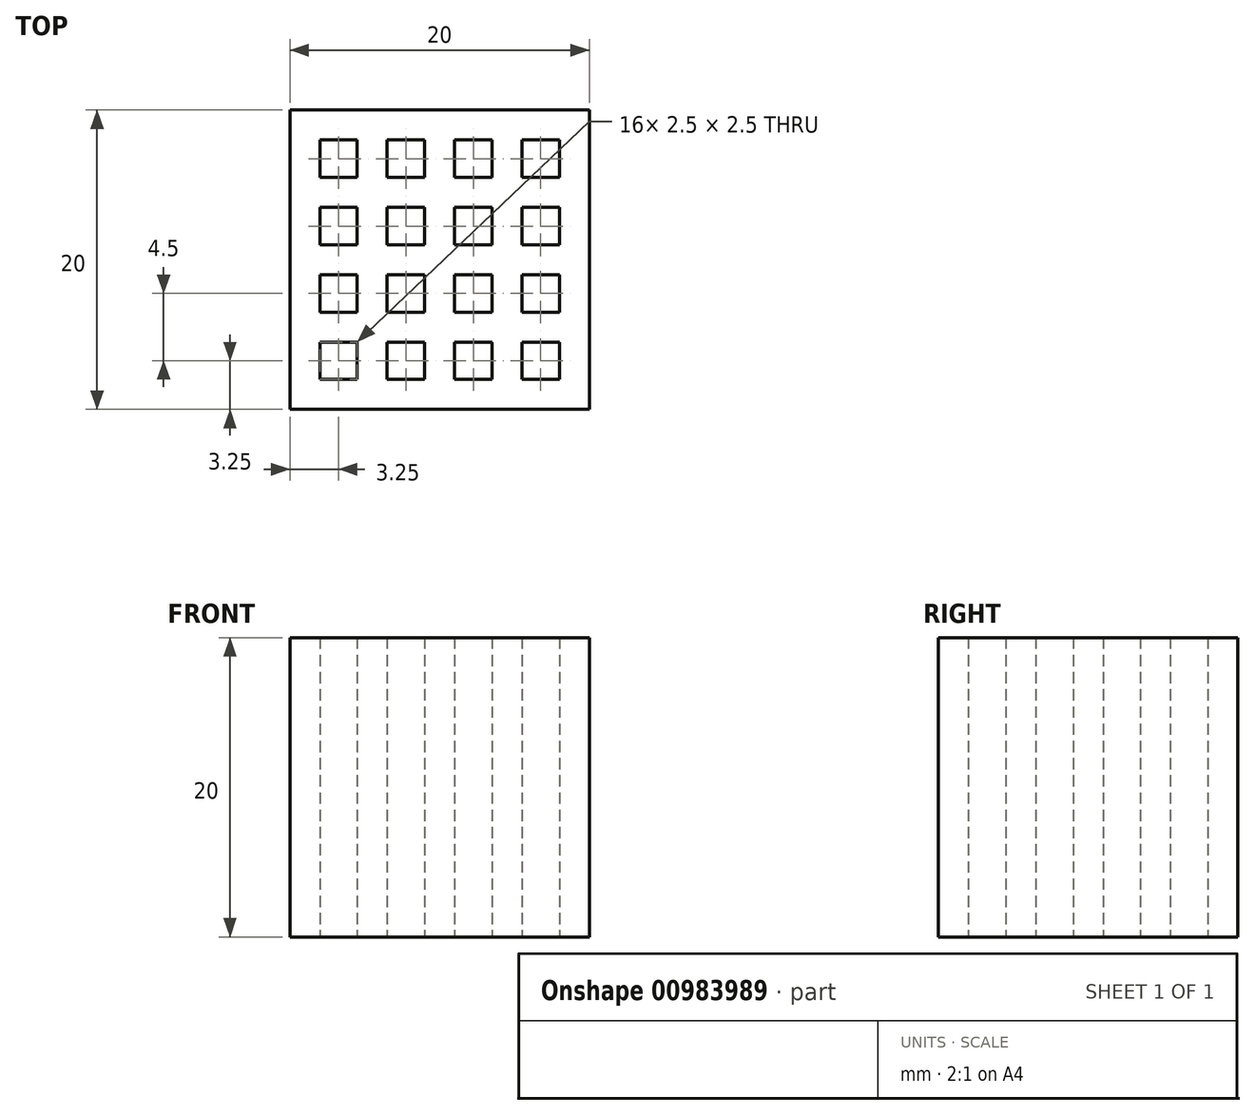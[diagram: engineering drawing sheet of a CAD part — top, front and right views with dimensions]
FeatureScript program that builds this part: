
annotation { "Feature Type Name" : "Feature", "Feature Type Description" : "" }
export const myFeature = defineFeature(function(context is Context, id is Id, definition is map)
    precondition{}
    {
        {
            var Q0;
            Q0=qCreatedBy(makeId("Top.planeOp"),FACE);
            var sketch = newSketch(context, id + "F0", { "sketchPlane" : qUnion([Q0])});
            skLineSegment(sketch, "E0.bottom", {"start": v(-8, -1) * mm, "end": v(-1, -1) * mm});
            skLineSegment(sketch, "E0.top", {"start": v(-8, -8) * mm, "end": v(-1, -8) * mm});
            skLineSegment(sketch, "E0.left", {"start": v(-8, -1) * mm, "end": v(-8, -8) * mm});
            skLineSegment(sketch, "E0.right", {"start": v(-1, -1) * mm, "end": v(-1, -8) * mm});
            skLineSegment(sketch, "E1.bottom", {"start": v(1, 8) * mm, "end": v(8, 8) * mm});
            skLineSegment(sketch, "E1.top", {"start": v(1, 1) * mm, "end": v(8, 1) * mm});
            skLineSegment(sketch, "E1.left", {"start": v(1, 8) * mm, "end": v(1, 1) * mm});
            skLineSegment(sketch, "E1.right", {"start": v(8, 8) * mm, "end": v(8, 1) * mm});
            skLineSegment(sketch, "E2.bottom", {"start": v(-10, 10) * mm, "end": v(10, 10) * mm});
            skLineSegment(sketch, "E2.top", {"start": v(-10, -10) * mm, "end": v(10, -10) * mm});
            skLineSegment(sketch, "E2.left", {"start": v(-10, 10) * mm, "end": v(-10, -10) * mm});
            skLineSegment(sketch, "E2.right", {"start": v(10, 10) * mm, "end": v(10, -10) * mm});
            skLineSegment(sketch, "E3", {"start": v(-8, 8) * mm, "end": v(-1, 8) * mm});
            skLineSegment(sketch, "E4", {"start": v(-1, 8) * mm, "end": v(-1, 1) * mm});
            skLineSegment(sketch, "E5", {"start": v(-1, 1) * mm, "end": v(-8, 1) * mm});
            skLineSegment(sketch, "E6", {"start": v(-8, 1) * mm, "end": v(-8, 8) * mm});
            skLineSegment(sketch, "E7", {"start": v(1, -1) * mm, "end": v(1, -8) * mm});
            skLineSegment(sketch, "E8", {"start": v(1, -8) * mm, "end": v(8, -8) * mm});
            skLineSegment(sketch, "E9", {"start": v(8, -8) * mm, "end": v(8, -1) * mm});
            skLineSegment(sketch, "E10", {"start": v(8, -1) * mm, "end": v(1, -1) * mm});
            skLineSegment(sketch, "E11", {"start": v(-8, -3.5) * mm, "end": v(-5.5, -3.5) * mm});
            skPoint(sketch, "E11.endSnap0", {"position": v(-1, -4.5) * mm});
            skLineSegment(sketch, "E12", {"start": v(-5.5, -8) * mm, "end": v(-5.5, -5.5) * mm});
            skPoint(sketch, "E12.endSnap0", {"position": v(-4.5, -1) * mm});
            skLineSegment(sketch, "E13", {"start": v(-8, -5.5) * mm, "end": v(-5.5, -5.5) * mm});
            skLineSegment(sketch, "E14", {"start": v(-3.5, -8) * mm, "end": v(-3.5, -5.5) * mm});
            skLineSegment(sketch, "E15.trimOffspring", {"start": v(-5.5, -3.5) * mm, "end": v(-5.5, -1) * mm});
            skLineSegment(sketch, "E16.trimOffspring", {"start": v(-3.5, -5.5) * mm, "end": v(-1, -5.5) * mm});
            skLineSegment(sketch, "E17.trimOffspring", {"start": v(-3.5, -3.5) * mm, "end": v(-3.5, -1) * mm});
            skLineSegment(sketch, "E18.trimOffspring", {"start": v(-3.5, -3.5) * mm, "end": v(-1, -3.5) * mm});
            skLineSegment(sketch, "E19", {"start": v(-8, 3.5) * mm, "end": v(-5.5, 3.5) * mm});
            skLineSegment(sketch, "E20", {"start": v(-8, 5.5) * mm, "end": v(-5.5, 5.5) * mm});
            skLineSegment(sketch, "E21", {"start": v(-5.5, 1) * mm, "end": v(-5.5, 3.5) * mm});
            skLineSegment(sketch, "E22", {"start": v(-3.5, 1) * mm, "end": v(-3.5, 3.5) * mm});
            skLineSegment(sketch, "E23.trimOffspring", {"start": v(-5.5, 5.5) * mm, "end": v(-5.5, 8) * mm});
            skLineSegment(sketch, "E24.trimOffspring", {"start": v(-3.5, 3.5) * mm, "end": v(-1, 3.5) * mm});
            skLineSegment(sketch, "E25.trimOffspring", {"start": v(-3.5, 5.5) * mm, "end": v(-3.5, 8) * mm});
            skLineSegment(sketch, "E26.trimOffspring", {"start": v(-3.5, 5.5) * mm, "end": v(-1, 5.5) * mm});
            skLineSegment(sketch, "E27", {"start": v(1, 3.5) * mm, "end": v(3.5, 3.5) * mm});
            skLineSegment(sketch, "E28", {"start": v(1, 5.5) * mm, "end": v(3.5, 5.5) * mm});
            skLineSegment(sketch, "E29", {"start": v(3.5, 1) * mm, "end": v(3.5, 3.5) * mm});
            skLineSegment(sketch, "E30", {"start": v(5.5, 1) * mm, "end": v(5.5, 3.5) * mm});
            skLineSegment(sketch, "E31", {"start": v(3.5, -8) * mm, "end": v(3.5, -5.5) * mm});
            skLineSegment(sketch, "E32", {"start": v(5.5, -8) * mm, "end": v(5.5, -5.5) * mm});
            skLineSegment(sketch, "E33", {"start": v(1, -5.5) * mm, "end": v(3.5, -5.5) * mm});
            skLineSegment(sketch, "E34", {"start": v(1, -3.5) * mm, "end": v(3.5, -3.5) * mm});
            skLineSegment(sketch, "E35.trimOffspring", {"start": v(3.5, -3.5) * mm, "end": v(3.5, -1) * mm});
            skLineSegment(sketch, "E36.trimOffspring", {"start": v(5.5, -3.5) * mm, "end": v(5.5, -1) * mm});
            skLineSegment(sketch, "E37.trimOffspring", {"start": v(5.5, -5.5) * mm, "end": v(8, -5.5) * mm});
            skLineSegment(sketch, "E38.trimOffspring", {"start": v(5.5, -3.5) * mm, "end": v(8, -3.5) * mm});
            skLineSegment(sketch, "E39.trimOffspring", {"start": v(5.5, 3.5) * mm, "end": v(8, 3.5) * mm});
            skLineSegment(sketch, "E40.trimOffspring", {"start": v(3.5, 5.5) * mm, "end": v(3.5, 8) * mm});
            skLineSegment(sketch, "E41.trimOffspring", {"start": v(5.5, 5.5) * mm, "end": v(5.5, 8) * mm});
            skLineSegment(sketch, "E42.trimOffspring", {"start": v(5.5, 5.5) * mm, "end": v(8, 5.5) * mm});
            skSolve(sketch);
        }
        {
            var Q0;
            Q0=makeQuery(id+"F0.imprint","IMPRINT",FACE,{"disambiguationData":[TD([[makeQuery(id+"F0.imprint","IMPRINT",EDGE,{"derivedFrom":sQuery(id+"F0.wireOp",EDGE,"E0.bottom")}),1.0]])]});
            var Q1;
            Q1=makeQuery(id+"F0.imprint","IMPRINT",FACE,{"disambiguationData":[TD([[makeQuery(id+"F0.imprint","IMPRINT",EDGE,{"derivedFrom":sQuery(id+"F0.wireOp",EDGE,"E0.bottom")}),-1.0]])]});
            var Q2;
            Q2=makeQuery(id+"F0.imprint","IMPRINT",FACE,{"disambiguationData":[TD([[makeQuery(id+"F0.imprint","IMPRINT",EDGE,{"derivedFrom":sQuery(id+"F0.wireOp",EDGE,"E7")}),1.0]])]});
            var Q3;
            Q3=makeQuery(id+"F0.imprint","IMPRINT",FACE,{"disambiguationData":[TD([[makeQuery(id+"F0.imprint","IMPRINT",EDGE,{"derivedFrom":sQuery(id+"F0.wireOp",EDGE,"E3")}),-1.0]])]});
            var Q4;
            Q4=makeQuery(id+"F0.imprint","IMPRINT",FACE,{"disambiguationData":[TD([[makeQuery(id+"F0.imprint","IMPRINT",EDGE,{"derivedFrom":sQuery(id+"F0.wireOp",EDGE,"E1.bottom")}),-1.0]])]});
            var Q5;
            {var subQ4=sQuery(id+"F0.wireOp",EDGE,"E19");Q5=makeQuery(id+"F0.imprint","IMPRINT",FACE,{"disambiguationData":[TD([[makeQuery(id+"F0.imprint","IMPRINT",EDGE,{"derivedFrom":subQ4}),-1.0]])]});}
            var Q6;
            {var subQ3=sQuery(id+"F0.wireOp",EDGE,"E19");Q6=makeQuery(id+"F0.imprint","IMPRINT",FACE,{"disambiguationData":[TD([[makeQuery(id+"F0.imprint","IMPRINT",EDGE,{"derivedFrom":subQ3}),1.0]])]});}
            var Q7;
            {var subQ4=sQuery(id+"F0.wireOp",EDGE,"E22");Q7=makeQuery(id+"F0.imprint","IMPRINT",FACE,{"disambiguationData":[TD([[makeQuery(id+"F0.imprint","IMPRINT",EDGE,{"derivedFrom":subQ4}),-1.0]])]});}
            var Q8;
            {var subQ4=sQuery(id+"F0.wireOp",EDGE,"E27");Q8=makeQuery(id+"F0.imprint","IMPRINT",FACE,{"disambiguationData":[TD([[makeQuery(id+"F0.imprint","IMPRINT",EDGE,{"derivedFrom":subQ4}),1.0]])]});}
            var Q9;
            {var subQ4=sQuery(id+"F0.wireOp",EDGE,"E27");Q9=makeQuery(id+"F0.imprint","IMPRINT",FACE,{"disambiguationData":[TD([[makeQuery(id+"F0.imprint","IMPRINT",EDGE,{"derivedFrom":subQ4}),-1.0]])]});}
            var Q10;
            {var subQ3=sQuery(id+"F0.wireOp",EDGE,"E30");Q10=makeQuery(id+"F0.imprint","IMPRINT",FACE,{"disambiguationData":[TD([[makeQuery(id+"F0.imprint","IMPRINT",EDGE,{"derivedFrom":subQ3}),-1.0]])]});}
            var Q11;
            {var subQ4=sQuery(id+"F0.wireOp",EDGE,"E36.trimOffspring");Q11=makeQuery(id+"F0.imprint","IMPRINT",FACE,{"disambiguationData":[TD([[makeQuery(id+"F0.imprint","IMPRINT",EDGE,{"derivedFrom":subQ4}),-1.0]])]});}
            var Q12;
            {var subQ3=sQuery(id+"F0.wireOp",EDGE,"E32");Q12=makeQuery(id+"F0.imprint","IMPRINT",FACE,{"disambiguationData":[TD([[makeQuery(id+"F0.imprint","IMPRINT",EDGE,{"derivedFrom":subQ3}),-1.0]])]});}
            var Q13;
            {var subQ7=sQuery(id+"F0.wireOp",EDGE,"E31");Q13=makeQuery(id+"F0.imprint","IMPRINT",FACE,{"disambiguationData":[TD([[makeQuery(id+"F0.imprint","IMPRINT",EDGE,{"derivedFrom":subQ7}),-1.0]])]});}
            var Q14;
            {var subQ3=sQuery(id+"F0.wireOp",EDGE,"E12");Q14=makeQuery(id+"F0.imprint","IMPRINT",FACE,{"disambiguationData":[TD([[makeQuery(id+"F0.imprint","IMPRINT",EDGE,{"derivedFrom":subQ3}),1.0]])]});}
            var Q15;
            {var subQ3=sQuery(id+"F0.wireOp",EDGE,"E11");Q15=makeQuery(id+"F0.imprint","IMPRINT",FACE,{"disambiguationData":[TD([[makeQuery(id+"F0.imprint","IMPRINT",EDGE,{"derivedFrom":subQ3}),-1.0]])]});}
            var Q16;
            {var subQ3=sQuery(id+"F0.wireOp",EDGE,"E14");Q16=makeQuery(id+"F0.imprint","IMPRINT",FACE,{"disambiguationData":[TD([[makeQuery(id+"F0.imprint","IMPRINT",EDGE,{"derivedFrom":subQ3}),-1.0]])]});}
            extrude(context, id + "F1", {"entities" : qUnion([Q0, Q1, Q2, Q3, Q4, Q5, Q6, Q7, Q8, Q9, Q10, Q11, Q12, Q13, Q14, Q15, Q16]), "endBound" : BoundingType.SYMMETRIC, "depth" : 20 * mm, "offsetDistance" : 25 * mm});
        }
        {
            var Q0;
            {var subQ4=sQuery(id+"F0.wireOp",EDGE,"E20");Q0=makeQuery(id+"F0.imprint","IMPRINT",FACE,{"disambiguationData":[TD([[makeQuery(id+"F0.imprint","IMPRINT",EDGE,{"derivedFrom":subQ4}),1.0]])]});}
            var Q1;
            {var subQ3=sQuery(id+"F0.wireOp",EDGE,"E25.trimOffspring");Q1=makeQuery(id+"F0.imprint","IMPRINT",FACE,{"disambiguationData":[TD([[makeQuery(id+"F0.imprint","IMPRINT",EDGE,{"derivedFrom":subQ3}),-1.0]])]});}
            var Q2;
            {var subQ4=sQuery(id+"F0.wireOp",EDGE,"E28");Q2=makeQuery(id+"F0.imprint","IMPRINT",FACE,{"disambiguationData":[TD([[makeQuery(id+"F0.imprint","IMPRINT",EDGE,{"derivedFrom":subQ4}),1.0]])]});}
            var Q3;
            {var subQ3=sQuery(id+"F0.wireOp",EDGE,"E30");Q3=makeQuery(id+"F0.imprint","IMPRINT",FACE,{"disambiguationData":[TD([[makeQuery(id+"F0.imprint","IMPRINT",EDGE,{"derivedFrom":subQ3}),-1.0]])]});}
            var Q4;
            {var subQ4=sQuery(id+"F0.wireOp",EDGE,"E27");Q4=makeQuery(id+"F0.imprint","IMPRINT",FACE,{"disambiguationData":[TD([[makeQuery(id+"F0.imprint","IMPRINT",EDGE,{"derivedFrom":subQ4}),-1.0]])]});}
            var Q5;
            {var subQ3=sQuery(id+"F0.wireOp",EDGE,"E41.trimOffspring");Q5=makeQuery(id+"F0.imprint","IMPRINT",FACE,{"disambiguationData":[TD([[makeQuery(id+"F0.imprint","IMPRINT",EDGE,{"derivedFrom":subQ3}),-1.0]])]});}
            var Q6;
            {var subQ4=sQuery(id+"F0.wireOp",EDGE,"E36.trimOffspring");Q6=makeQuery(id+"F0.imprint","IMPRINT",FACE,{"disambiguationData":[TD([[makeQuery(id+"F0.imprint","IMPRINT",EDGE,{"derivedFrom":subQ4}),-1.0]])]});}
            var Q7;
            {var subQ3=sQuery(id+"F0.wireOp",EDGE,"E32");Q7=makeQuery(id+"F0.imprint","IMPRINT",FACE,{"disambiguationData":[TD([[makeQuery(id+"F0.imprint","IMPRINT",EDGE,{"derivedFrom":subQ3}),-1.0]])]});}
            var Q8;
            {var subQ4=sQuery(id+"F0.wireOp",EDGE,"E31");Q8=makeQuery(id+"F0.imprint","IMPRINT",FACE,{"disambiguationData":[TD([[makeQuery(id+"F0.imprint","IMPRINT",EDGE,{"derivedFrom":subQ4}),1.0]])]});}
            var Q9;
            {var subQ3=sQuery(id+"F0.wireOp",EDGE,"E34");Q9=makeQuery(id+"F0.imprint","IMPRINT",FACE,{"disambiguationData":[TD([[makeQuery(id+"F0.imprint","IMPRINT",EDGE,{"derivedFrom":subQ3}),1.0]])]});}
            var Q10;
            {var subQ4=sQuery(id+"F0.wireOp",EDGE,"E22");Q10=makeQuery(id+"F0.imprint","IMPRINT",FACE,{"disambiguationData":[TD([[makeQuery(id+"F0.imprint","IMPRINT",EDGE,{"derivedFrom":subQ4}),-1.0]])]});}
            var Q11;
            {var subQ4=sQuery(id+"F0.wireOp",EDGE,"E19");Q11=makeQuery(id+"F0.imprint","IMPRINT",FACE,{"disambiguationData":[TD([[makeQuery(id+"F0.imprint","IMPRINT",EDGE,{"derivedFrom":subQ4}),-1.0]])]});}
            var Q12;
            {var subQ4=sQuery(id+"F0.wireOp",EDGE,"E11");Q12=makeQuery(id+"F0.imprint","IMPRINT",FACE,{"disambiguationData":[TD([[makeQuery(id+"F0.imprint","IMPRINT",EDGE,{"derivedFrom":subQ4}),1.0]])]});}
            var Q13;
            {var subQ3=sQuery(id+"F0.wireOp",EDGE,"E17.trimOffspring");Q13=makeQuery(id+"F0.imprint","IMPRINT",FACE,{"disambiguationData":[TD([[makeQuery(id+"F0.imprint","IMPRINT",EDGE,{"derivedFrom":subQ3}),-1.0]])]});}
            var Q14;
            {var subQ3=sQuery(id+"F0.wireOp",EDGE,"E14");Q14=makeQuery(id+"F0.imprint","IMPRINT",FACE,{"disambiguationData":[TD([[makeQuery(id+"F0.imprint","IMPRINT",EDGE,{"derivedFrom":subQ3}),-1.0]])]});}
            var Q15;
            {var subQ3=sQuery(id+"F0.wireOp",EDGE,"E12");Q15=makeQuery(id+"F0.imprint","IMPRINT",FACE,{"disambiguationData":[TD([[makeQuery(id+"F0.imprint","IMPRINT",EDGE,{"derivedFrom":subQ3}),1.0]])]});}
            extrude(context, id + "F2", {"entities" : qUnion([Q0, Q1, Q2, Q3, Q4, Q5, Q6, Q7, Q8, Q9, Q10, Q11, Q12, Q13, Q14, Q15]), "operationType" : NewBodyOperationType.REMOVE, "endBound" : BoundingType.SYMMETRIC, "depth" : 30 * mm, "offsetDistance" : 25 * mm});
        }
        {
            var Q0;
            Q0=makeQuery(id+"F0.imprint","IMPRINT",FACE,{"disambiguationData":[TD([[makeQuery(id+"F0.imprint","IMPRINT",EDGE,{"derivedFrom":sQuery(id+"F0.wireOp",EDGE,"E7")}),1.0]])]});
            var Q1;
            Q1=makeQuery(id+"F0.imprint","IMPRINT",FACE,{"disambiguationData":[TD([[makeQuery(id+"F0.imprint","IMPRINT",EDGE,{"derivedFrom":sQuery(id+"F0.wireOp",EDGE,"E1.bottom")}),-1.0]])]});
            var Q2;
            Q2=makeQuery(id+"F0.imprint","IMPRINT",FACE,{"disambiguationData":[TD([[makeQuery(id+"F0.imprint","IMPRINT",EDGE,{"derivedFrom":sQuery(id+"F0.wireOp",EDGE,"E3")}),-1.0]])]});
            var Q3;
            Q3=makeQuery(id+"F0.imprint","IMPRINT",FACE,{"disambiguationData":[TD([[makeQuery(id+"F0.imprint","IMPRINT",EDGE,{"derivedFrom":sQuery(id+"F0.wireOp",EDGE,"E0.bottom")}),-1.0]])]});
            extrude(context, id + "F3", {"entities" : qUnion([Q0, Q1, Q2, Q3]), "operationType" : NewBodyOperationType.REMOVE, "endBound" : BoundingType.SYMMETRIC, "oppositeDirection" : true, "depth" : 20 * mm, "offsetDistance" : 25 * mm});
        }
        {
            var Q0;
            Q0=makeQuery(id+"F1.opExtrude","CAP_VERTEX",VERTEX,{"disambiguationData":[OSD([sQuery(id+"F0.wireOp",EDGE,"E2.top"),sQuery(id+"F0.wireOp",EDGE,"E2.right")])],"isStart":true});
            var Q1;
            Q1=makeQuery(id+"F1.opExtrude","CAP_VERTEX",VERTEX,{"disambiguationData":[OSD([sQuery(id+"F0.wireOp",EDGE,"E2.bottom"),sQuery(id+"F0.wireOp",EDGE,"E2.left")])],"isStart":false});
            var Q2;
            Q2=makeQuery(id+"F1.opExtrude","CAP_VERTEX",VERTEX,{"disambiguationData":[OSD([sQuery(id+"F0.wireOp",EDGE,"E2.bottom"),sQuery(id+"F0.wireOp",EDGE,"E2.left")])],"isStart":true});
            cPlane(context, id + "F4", {"entities" : qUnion([Q0, Q1, Q2]), "cplaneType" : CPlaneType.THREE_POINT, "offset" : 25 * mm, "width" : 150 * mm, "height" : 150 * mm});
        }
        {
            var Q0;
            Q0=qCreatedBy(id+"F4.planeOp",FACE);
            var sketch = newSketch(context, id + "F5", { "sketchPlane" : qUnion([Q0])});
            skPoint(sketch, "E43.0", {"position": v(-14.14, -10) * mm});
            skPoint(sketch, "E44.0", {"position": v(14.14, 10) * mm});
            skLineSegment(sketch, "E45", {"start": v(-14.14, -10) * mm, "end": v(14.14, 10) * mm});
            skSolve(sketch);
        }
    });
